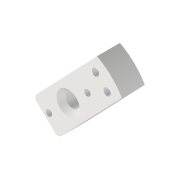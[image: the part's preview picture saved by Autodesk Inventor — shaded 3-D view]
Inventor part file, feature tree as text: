
AUTODESK INVENTOR PART (.ipt)
format: ipt  version: 2022 (Build 260153000, 153)  size: 132,608 bytes
history: native  units: mm
features: reference x5, other x5, sketch x3, extrude x1, chamfer x1, fillet x1
ambient origin geometry x8: Origin, YZ Plane, XZ Plane, XY Plane, X Axis, Y Axis, Z Axis, Center Point
bodies: Volumenkörper1 (feature_tree)
feature tree (16):
  extrude  "Extrusion1"  Depth=6.2mm
  sketch  "Skizze2"  dims[d2=3.2mm]
  sketch  "Skizze3"  dims[d3=3.2mm d4=10.0mm d5=0.0mm d6=2.0mm d7=2.0mm d8=45.0deg d9=2.0mm]
  chamfer  "Fase1"  Distance=10.0mm
  fillet  "Rundung1"  Radius=2.0mm
  sketch  "Skizze1"  dims[d0=30.0mm d1=6.2mm]
  reference  "Referenz1"
  reference  "Referenz2"
  reference  "Referenz3"
  reference  "Referenz4"
  reference  "Referenz5"
  other  "Assembly_Matchboxscope_injectionmolded_holo.iam"
  other  "IM_Matchboxscope_Laserholder:1"
  other  "00_laserpointer_red:2"
  other  "00_mk8_nozzle_0.4STEP:1"
  other  "IM_Lensholder:1"
